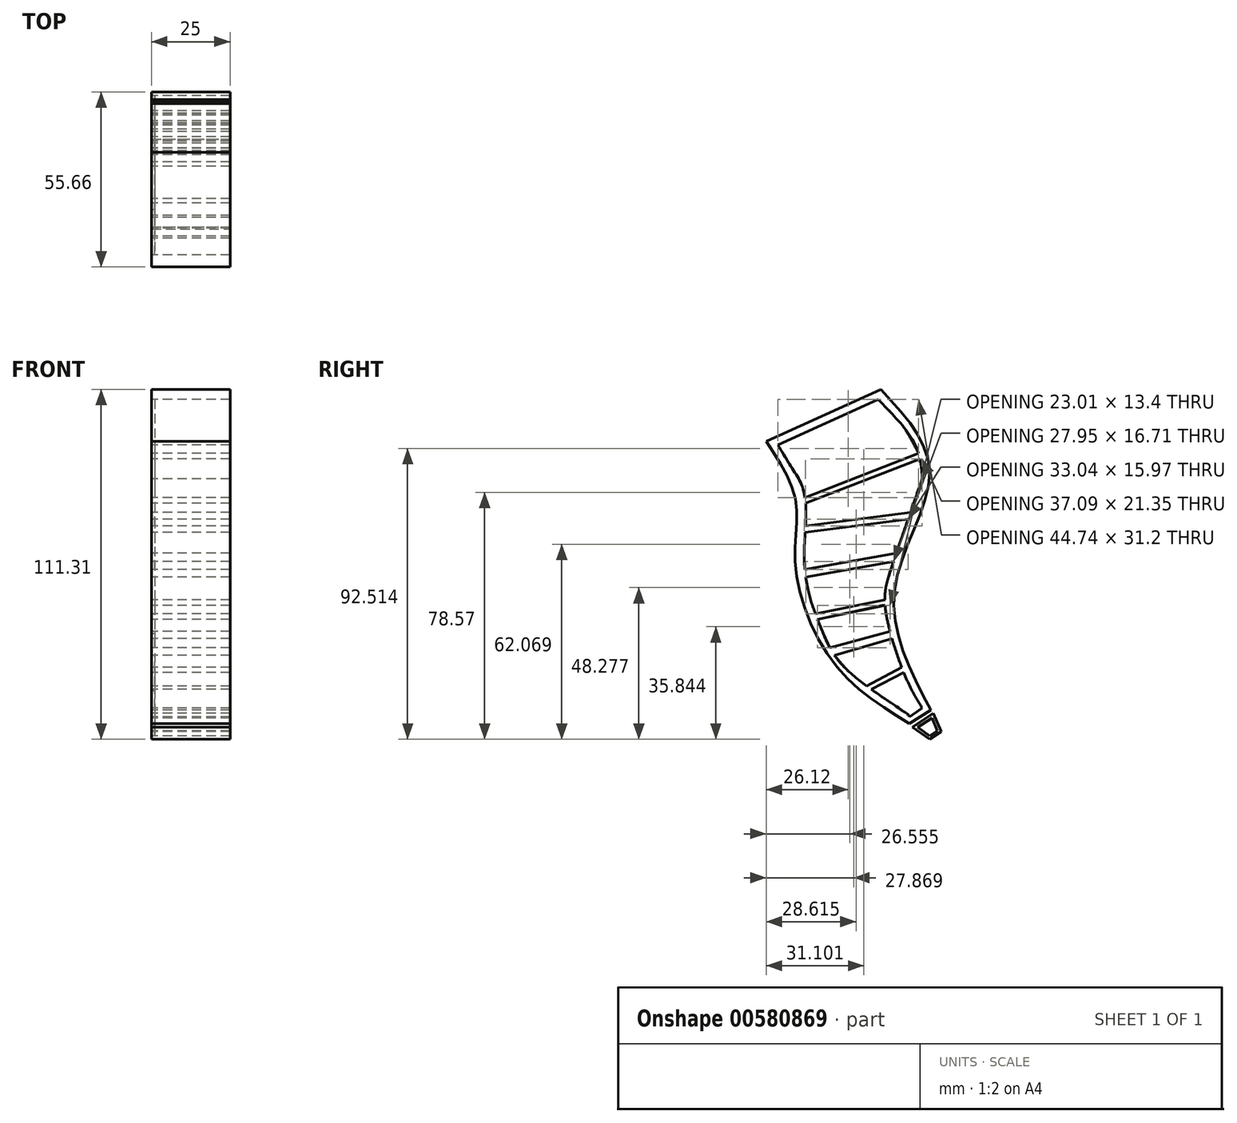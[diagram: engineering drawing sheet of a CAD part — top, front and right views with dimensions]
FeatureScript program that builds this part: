
annotation { "Feature Type Name" : "Feature", "Feature Type Description" : "" }
export const myFeature = defineFeature(function(context is Context, id is Id, definition is map)
    precondition{}
    {
        {
            var Q0;
            Q0=qCreatedBy(makeId("Right.planeOp"),FACE);
            var sketch = newSketch(context, id + "F0", { "sketchPlane" : qUnion([Q0])});
            skLineSegment(sketch, "E0", {"start": v(40.35, 35.98) * mm, "end": v(76.8, 52.44) * mm});
            skFitSpline(sketch, "E1", {"points": [v(40.35, 35.98) * mm, v(49.78, 17) * mm, v(49.59, -3.47) * mm, v(62.3, -35.09) * mm, v(85.9, -53.8) * mm], "startDerivative": vector(55.56, -83.92) * mm, "endDerivative": vector(95.14, -57.57) * mm});
            skFitSpline(sketch, "E2", {"points": [v(76.8, 52.44) * mm, v(92.3, 25.95) * mm, v(81.18, -11.43) * mm, v(92.7, -49.6) * mm], "startDerivative": vector(75.58, -81.14) * mm, "endDerivative": vector(56.5, -108.15) * mm});
            skLineSegment(sketch, "E3", {"start": v(85.9, -53.8) * mm, "end": v(92.7, -49.6) * mm});
            skLineSegment(sketch, "E4", {"start": v(44.1, 34.77) * mm, "end": v(75.97, 49.24) * mm});
            skFitSpline(sketch, "E5", {"points": [v(75.97, 49.24) * mm, v(87.81, 34.77) * mm, v(90, 24.03) * mm], "startDerivative": vector(25.4, -25.78) * mm, "endDerivative": vector(1.6, -24.6) * mm});
            skFitSpline(sketch, "E6", {"points": [v(90, 24.03) * mm, v(84.83, 9.32) * mm, v(79.67, -5.99) * mm, v(78.08, -14.54) * mm, v(80.86, -28.46) * mm, v(86.22, -42.37) * mm, v(90, -48.93) * mm], "startDerivative": vector(-27.15, -77) * mm, "endDerivative": vector(28.72, -45.43) * mm});
            skPoint(sketch, "E7.9.internal.snap0", {"position": v(89.3, -51.7) * mm});
            skFitSpline(sketch, "E7", {"points": [v(44.1, 34.77) * mm, v(48.47, 27.58) * mm, v(51.65, 22.04) * mm, v(53.04, 13.3) * mm, v(52.45, 0) * mm, v(54.04, -12.75) * mm, v(58.2, -24.48) * mm, v(66.75, -37.4) * mm, v(85.83, -51.32) * mm, v(86, -51.7) * mm], "startDerivative": vector(43.93, -74.3) * mm, "endDerivative": vector(0.94, -12.08) * mm});
            skFitSpline(sketch, "E8", {"points": [v(90, -48.93) * mm, v(86, -51.7) * mm], "startDerivative": vector(-3.97, -2.75) * mm, "endDerivative": vector(-3.97, -2.75) * mm});
            skLineSegment(sketch, "E9", {"start": v(73.75, -42.93) * mm, "end": v(84.1, -37.61) * mm});
            skLineSegment(sketch, "E10", {"start": v(72.29, -41.86) * mm, "end": v(83.45, -35.94) * mm});
            skLineSegment(sketch, "E11", {"start": v(52.9, 9.03) * mm, "end": v(86.22, 13.3) * mm});
            skLineSegment(sketch, "E12", {"start": v(52.78, 7) * mm, "end": v(85.48, 11.18) * mm});
            skLineSegment(sketch, "E13", {"start": v(60.61, -29.72) * mm, "end": v(79.72, -24.5) * mm});
            skLineSegment(sketch, "E14", {"start": v(62.1, -32.13) * mm, "end": v(80.38, -26.86) * mm});
            skLineSegment(sketch, "E15", {"start": v(52.9, 16.24) * mm, "end": v(89.27, 30.37) * mm});
            skLineSegment(sketch, "E16", {"start": v(52.69, 18.05) * mm, "end": v(88.84, 32.1) * mm});
            skLineSegment(sketch, "E17", {"start": v(86.87, -55) * mm, "end": v(93.55, -50.59) * mm});
            skLineSegment(sketch, "E18", {"start": v(86.87, -55) * mm, "end": v(92.3, -58.87) * mm});
            skLineSegment(sketch, "E19", {"start": v(92.3, -58.87) * mm, "end": v(96, -56.42) * mm});
            skLineSegment(sketch, "E20", {"start": v(96, -56.42) * mm, "end": v(93.55, -50.59) * mm});
            skLineSegment(sketch, "E21", {"start": v(88.55, -55) * mm, "end": v(93.06, -52.02) * mm});
            skLineSegment(sketch, "E22", {"start": v(93.06, -52.02) * mm, "end": v(94.8, -56.16) * mm});
            skLineSegment(sketch, "E23", {"start": v(94.8, -56.16) * mm, "end": v(92.3, -57.8) * mm});
            skLineSegment(sketch, "E24", {"start": v(92.3, -57.8) * mm, "end": v(88.55, -55) * mm});
            skLineSegment(sketch, "E25", {"start": v(52.93, -7.22) * mm, "end": v(80.88, -2.24) * mm});
            skLineSegment(sketch, "E26", {"start": v(52.65, -4.79) * mm, "end": v(81.76, 0.4) * mm});
            skLineSegment(sketch, "E27", {"start": v(56.71, -20.77) * mm, "end": v(77.27, -16.33) * mm});
            skLineSegment(sketch, "E28", {"start": v(56.02, -18.95) * mm, "end": v(78.08, -14.54) * mm});
            skLineSegment(sketch, "E29", {"start": v(77.27, -16.33) * mm, "end": v(78.17, -16.33) * mm});
            skSolve(sketch);
        }
        {
            var Q0;
            Q0 = qSketchRegion(id + "F0", true);
            extrude(context, id + "F1", {"entities" : qUnion([Q0]), "depth" : 25 * mm, "offsetDistance" : 25 * mm});
        }
        {
            var Q0;
            {var subQ0=sQuery(id+"F0.wireOp",EDGE,"E15");Q0=makeQuery(id+"F0.imprint","IMPRINT",FACE,{"disambiguationData":[TD([[makeQuery(id+"F0.imprint","IMPRINT",EDGE,{"derivedFrom":subQ0}),1.0]])]});}
            extrude(context, id + "F2", {"entities" : qUnion([Q0]), "operationType" : NewBodyOperationType.ADD, "depth" : 25 * mm, "offsetDistance" : 25 * mm});
        }
        {
            var Q0;
            {var subQ0=sQuery(id+"F0.wireOp",EDGE,"E11");Q0=makeQuery(id+"F0.imprint","IMPRINT",FACE,{"disambiguationData":[TD([[makeQuery(id+"F0.imprint","IMPRINT",EDGE,{"derivedFrom":subQ0}),-1.0]])]});}
            extrude(context, id + "F3", {"entities" : qUnion([Q0]), "operationType" : NewBodyOperationType.ADD, "depth" : 25 * mm, "offsetDistance" : 25 * mm});
        }
        {
            var Q0;
            {var subQ0=sQuery(id+"F0.wireOp",EDGE,"E25");Q0=makeQuery(id+"F0.imprint","IMPRINT",FACE,{"disambiguationData":[TD([[makeQuery(id+"F0.imprint","IMPRINT",EDGE,{"derivedFrom":subQ0}),1.0]])]});}
            extrude(context, id + "F4", {"entities" : qUnion([Q0]), "operationType" : NewBodyOperationType.ADD, "depth" : 25 * mm, "offsetDistance" : 25 * mm});
        }
        {
            var Q0;
            {var subQ1=sQuery(id+"F0.wireOp",EDGE,"E27");Q0=makeQuery(id+"F0.imprint","IMPRINT",FACE,{"disambiguationData":[TD([[makeQuery(id+"F0.imprint","IMPRINT",EDGE,{"derivedFrom":subQ1}),1.0]])]});}
            extrude(context, id + "F5", {"entities" : qUnion([Q0]), "operationType" : NewBodyOperationType.ADD, "depth" : 25 * mm, "offsetDistance" : 25 * mm});
        }
        {
            var Q0;
            {var subQ0=sQuery(id+"F0.wireOp",EDGE,"E13");Q0=makeQuery(id+"F0.imprint","IMPRINT",FACE,{"disambiguationData":[TD([[makeQuery(id+"F0.imprint","IMPRINT",EDGE,{"derivedFrom":subQ0}),-1.0]])]});}
            extrude(context, id + "F6", {"entities" : qUnion([Q0]), "operationType" : NewBodyOperationType.ADD, "depth" : 25 * mm, "offsetDistance" : 25 * mm});
        }
        {
            var Q0;
            {var subQ0=sQuery(id+"F0.wireOp",EDGE,"E9");Q0=makeQuery(id+"F0.imprint","IMPRINT",FACE,{"disambiguationData":[TD([[makeQuery(id+"F0.imprint","IMPRINT",EDGE,{"derivedFrom":subQ0}),1.0]])]});}
            extrude(context, id + "F7", {"entities" : qUnion([Q0]), "operationType" : NewBodyOperationType.ADD, "depth" : 25 * mm, "offsetDistance" : 25 * mm});
        }
        {
            var Q0;
            {var subQ0=sQuery(id+"F0.wireOp",EDGE,"E7");var subQ1=sQuery(id+"F0.wireOp",EDGE,"E6");var subQ2=sQuery(id+"F0.wireOp",EDGE,"E5");Q0=makeQuery(id+"F7.boolean.opBoolean","MERGE",FACE,{"derivedFrom":[makeQuery(id+"F6.boolean.opBoolean","MERGE",FACE,{"derivedFrom":[makeQuery(id+"F5.boolean.opBoolean","MERGE",FACE,{"derivedFrom":[makeQuery(id+"F4.boolean.opBoolean","MERGE",FACE,{"derivedFrom":[makeQuery(id+"F3.boolean.opBoolean","MERGE",FACE,{"derivedFrom":[makeQuery(id+"F2.boolean.opBoolean","MERGE",FACE,{"derivedFrom":[makeQuery(id+"F1.opExtrude","CAP_FACE",FACE,{"disambiguationData":[OSD([sQuery(id+"F0.wireOp",EDGE,"E0"),sQuery(id+"F0.wireOp",EDGE,"E1"),sQuery(id+"F0.wireOp",EDGE,"E2"),sQuery(id+"F0.wireOp",EDGE,"E3"),sQuery(id+"F0.wireOp",EDGE,"E4"),subQ2,subQ1,subQ0,sQuery(id+"F0.wireOp",EDGE,"E8")])],"isStart":true}),makeQuery(id+"F2.opExtrude","CAP_FACE",FACE,{"disambiguationData":[OSD([subQ2,subQ0,sQuery(id+"F0.wireOp",EDGE,"E15"),sQuery(id+"F0.wireOp",EDGE,"E16")])],"isStart":true})]}),makeQuery(id+"F3.opExtrude","CAP_FACE",FACE,{"disambiguationData":[OSD([subQ1,subQ0,sQuery(id+"F0.wireOp",EDGE,"E11"),sQuery(id+"F0.wireOp",EDGE,"E12")])],"isStart":true})]}),makeQuery(id+"F4.opExtrude","CAP_FACE",FACE,{"disambiguationData":[OSD([subQ1,subQ0,sQuery(id+"F0.wireOp",EDGE,"E25"),sQuery(id+"F0.wireOp",EDGE,"E26")])],"isStart":true})]}),makeQuery(id+"F5.opExtrude","CAP_FACE",FACE,{"disambiguationData":[OSD([subQ1,subQ0,sQuery(id+"F0.wireOp",EDGE,"E27"),sQuery(id+"F0.wireOp",EDGE,"E28"),sQuery(id+"F0.wireOp",EDGE,"E29")])],"isStart":true})]}),makeQuery(id+"F6.opExtrude","CAP_FACE",FACE,{"disambiguationData":[OSD([subQ1,subQ0,sQuery(id+"F0.wireOp",EDGE,"E13"),sQuery(id+"F0.wireOp",EDGE,"E14")])],"isStart":true})]}),makeQuery(id+"F7.opExtrude","CAP_FACE",FACE,{"disambiguationData":[OSD([subQ1,subQ0,sQuery(id+"F0.wireOp",EDGE,"E9"),sQuery(id+"F0.wireOp",EDGE,"E10")])],"isStart":true})]});}
            cPlane(context, id + "F8", {"entities" : qUnion([Q0]), "cplaneType" : CPlaneType.OFFSET, "offset" : 0 * mm, "width" : 150 * mm, "height" : 150 * mm});
        }
        {
            var Q0;
            Q0=qCreatedBy(id+"F8.planeOp",FACE);
            var sketch = newSketch(context, id + "F9", { "sketchPlane" : qUnion([Q0])});
            skPoint(sketch, "E30.0", {"position": v(-49.06, 26.7) * mm});
            skPoint(sketch, "E31.0", {"position": v(-75.97, 49.24) * mm});
            skPoint(sketch, "E32.0", {"position": v(-44.1, 34.77) * mm});
            skPoint(sketch, "E33.0", {"position": v(-52.69, 18.05) * mm});
            skPoint(sketch, "E34.0", {"position": v(-88.84, 32.1) * mm});
            skPoint(sketch, "E35.0", {"position": v(-89.27, 30.37) * mm});
            skPoint(sketch, "E36.0", {"position": v(-86.22, 13.3) * mm});
            skPoint(sketch, "E37.0", {"position": v(-52.9, 9.03) * mm});
            skPoint(sketch, "E38.0", {"position": v(-52.9, 16.24) * mm});
            skFitSpline(sketch, "E39", {"points": [v(-75.97, 49.24) * mm, v(-83.51, 41.21) * mm, v(-88.84, 32.1) * mm], "startDerivative": vector(-15.99, -15.24) * mm, "endDerivative": vector(-9.73, -19.07) * mm});
            skFitSpline(sketch, "E40", {"points": [v(-75.97, 49.24) * mm, v(-44.1, 34.77) * mm], "startDerivative": vector(31.87, -14.48) * mm, "endDerivative": vector(31.87, -14.48) * mm});
            skFitSpline(sketch, "E41", {"points": [v(-44.1, 34.77) * mm, v(-49.06, 26.7) * mm, v(-51.59, 22.32) * mm, v(-52.69, 18.05) * mm], "startDerivative": vector(-12.7, -21.07) * mm, "endDerivative": vector(-2.96, -15.55) * mm});
            skFitSpline(sketch, "E42", {"points": [v(-88.84, 32.1) * mm, v(-52.69, 18.05) * mm], "startDerivative": vector(36.15, -14.05) * mm, "endDerivative": vector(36.15, -14.05) * mm});
            skFitSpline(sketch, "E43", {"points": [v(-89.27, 30.37) * mm, v(-90.25, 24.39) * mm, v(-86.22, 13.3) * mm], "startDerivative": vector(-4.27, -13.36) * mm, "endDerivative": vector(9.61, -20.41) * mm});
            skFitSpline(sketch, "E44", {"points": [v(-89.27, 30.37) * mm, v(-52.9, 16.24) * mm], "startDerivative": vector(36.37, -14.13) * mm, "endDerivative": vector(36.37, -14.13) * mm});
            skFitSpline(sketch, "E45", {"points": [v(-52.9, 9.03) * mm, v(-86.22, 13.3) * mm], "startDerivative": vector(-33.32, 4.27) * mm, "endDerivative": vector(-33.32, 4.27) * mm});
            skFitSpline(sketch, "E46", {"points": [v(-52.9, 16.24) * mm, v(-52.9, 9.03) * mm], "startDerivative": vector(0, -7.22) * mm, "endDerivative": vector(0, -7.22) * mm});
            skPoint(sketch, "E47.0", {"position": v(-52.78, 7) * mm});
            skPoint(sketch, "E48.0", {"position": v(-52.46, 1.1) * mm});
            skPoint(sketch, "E49.0", {"position": v(-52.65, -4.79) * mm});
            skPoint(sketch, "E50.0", {"position": v(-81.76, 0.4) * mm});
            skPoint(sketch, "E51.0", {"position": v(-85.48, 11.18) * mm});
            skPoint(sketch, "E52.0", {"position": v(-69.13, 9.09) * mm});
            skPoint(sketch, "E53.0", {"position": v(-80.88, -2.24) * mm});
            skPoint(sketch, "E54.0", {"position": v(-78.98, -8.29) * mm});
            skPoint(sketch, "E55.0", {"position": v(-78.08, -14.54) * mm});
            skPoint(sketch, "E56.0", {"position": v(-56.02, -18.95) * mm});
            skPoint(sketch, "E57.0", {"position": v(-54.15, -13.17) * mm});
            skPoint(sketch, "E58.0", {"position": v(-52.93, -7.22) * mm});
            skPoint(sketch, "E59.0", {"position": v(-78.17, -16.33) * mm});
            skPoint(sketch, "E60.0", {"position": v(-56.71, -20.77) * mm});
            skPoint(sketch, "E61.0", {"position": v(-60.61, -29.72) * mm});
            skPoint(sketch, "E62.0", {"position": v(-58.55, -25.3) * mm});
            skPoint(sketch, "E63.0", {"position": v(-78.78, -20.44) * mm});
            skPoint(sketch, "E64.0", {"position": v(-79.72, -24.5) * mm});
            skPoint(sketch, "E65.0", {"position": v(-80.38, -26.86) * mm});
            skPoint(sketch, "E66.0", {"position": v(-62.1, -32.13) * mm});
            skPoint(sketch, "E67.0", {"position": v(-66.78, -37.42) * mm});
            skPoint(sketch, "E68.0", {"position": v(-72.29, -41.86) * mm});
            skPoint(sketch, "E69.0", {"position": v(-83.45, -35.94) * mm});
            skPoint(sketch, "E70.0", {"position": v(-84.1, -37.61) * mm});
            skPoint(sketch, "E71.0", {"position": v(-73.75, -42.93) * mm});
            skPoint(sketch, "E72.0", {"position": v(-90, -48.93) * mm});
            skPoint(sketch, "E73.0", {"position": v(-86, -51.7) * mm});
            skPoint(sketch, "E74.0", {"position": v(-80, -47.2) * mm});
            skPoint(sketch, "E75.0", {"position": v(-86.76, -43.43) * mm});
            skPoint(sketch, "E76.0", {"position": v(-93.06, -52.02) * mm});
            skPoint(sketch, "E77.0", {"position": v(-88.55, -55) * mm});
            skPoint(sketch, "E78.0", {"position": v(-92.3, -57.8) * mm});
            skPoint(sketch, "E79.0", {"position": v(-94.8, -56.16) * mm});
            skFitSpline(sketch, "E80", {"points": [v(-85.48, 11.18) * mm, v(-81.76, 0.4) * mm], "startDerivative": vector(3.72, -10.78) * mm, "endDerivative": vector(3.72, -10.78) * mm});
            skFitSpline(sketch, "E81", {"points": [v(-52.65, -4.79) * mm, v(-81.76, 0.4) * mm], "startDerivative": vector(-29.11, 5.19) * mm, "endDerivative": vector(-29.11, 5.19) * mm});
            skFitSpline(sketch, "E82", {"points": [v(-85.48, 11.18) * mm, v(-52.78, 7) * mm], "startDerivative": vector(32.7, -4.2) * mm, "endDerivative": vector(32.7, -4.2) * mm});
            skFitSpline(sketch, "E83", {"points": [v(-52.78, 7) * mm, v(-52.46, 1.1) * mm, v(-52.65, -4.79) * mm], "startDerivative": vector(0.87, -11.77) * mm, "endDerivative": vector(-0.62, -11.78) * mm});
            skFitSpline(sketch, "E84", {"points": [v(-80.88, -2.24) * mm, v(-52.93, -7.22) * mm], "startDerivative": vector(27.95, -4.98) * mm, "endDerivative": vector(27.95, -4.98) * mm});
            skFitSpline(sketch, "E85", {"points": [v(-52.93, -7.22) * mm, v(-54.15, -13.17) * mm, v(-56.02, -19.11) * mm], "startDerivative": vector(-2.14, -12.02) * mm, "endDerivative": vector(-4.05, -11.77) * mm});
            skFitSpline(sketch, "E86", {"points": [v(-80.88, -2.24) * mm, v(-78.98, -8.29) * mm, v(-78.08, -14.54) * mm], "startDerivative": vector(4.3, -11.98) * mm, "endDerivative": vector(1.3, -12.63) * mm});
            skFitSpline(sketch, "E87", {"points": [v(-78.08, -14.54) * mm, v(-56.02, -18.95) * mm], "startDerivative": vector(22.05, -4.41) * mm, "endDerivative": vector(22.05, -4.41) * mm});
            skFitSpline(sketch, "E88", {"points": [v(-78.17, -16.33) * mm, v(-56.71, -20.77) * mm], "startDerivative": vector(21.46, -4.44) * mm, "endDerivative": vector(21.46, -4.44) * mm});
            skFitSpline(sketch, "E89", {"points": [v(-78.17, -16.33) * mm, v(-79.72, -24.5) * mm], "startDerivative": vector(-1.55, -8.17) * mm, "endDerivative": vector(-1.55, -8.17) * mm});
            skFitSpline(sketch, "E90", {"points": [v(-79.72, -24.5) * mm, v(-60.61, -29.72) * mm], "startDerivative": vector(19.1, -5.22) * mm, "endDerivative": vector(19.1, -5.22) * mm});
            skFitSpline(sketch, "E91", {"points": [v(-56.71, -20.77) * mm, v(-58.55, -25.3) * mm], "startDerivative": vector(-1.83, -4.53) * mm, "endDerivative": vector(-1.83, -4.53) * mm});
            skFitSpline(sketch, "E92", {"points": [v(-60.61, -29.72) * mm, v(-58.55, -25.3) * mm], "startDerivative": vector(2.07, 4.43) * mm, "endDerivative": vector(2.07, 4.43) * mm});
            skFitSpline(sketch, "E93", {"points": [v(-80.38, -26.86) * mm, v(-83.45, -35.94) * mm], "startDerivative": vector(-3.07, -9.08) * mm, "endDerivative": vector(-3.07, -9.08) * mm});
            skFitSpline(sketch, "E94", {"points": [v(-83.45, -35.94) * mm, v(-72.29, -41.86) * mm], "startDerivative": vector(11.16, -5.92) * mm, "endDerivative": vector(11.16, -5.92) * mm});
            skFitSpline(sketch, "E95", {"points": [v(-72.29, -41.86) * mm, v(-66.78, -37.42) * mm, v(-62.1, -32.13) * mm], "startDerivative": vector(11.42, 8.46) * mm, "endDerivative": vector(8.96, 11) * mm});
            skFitSpline(sketch, "E96", {"points": [v(-80.38, -26.86) * mm, v(-62.1, -32.13) * mm], "startDerivative": vector(18.28, -5.27) * mm, "endDerivative": vector(18.28, -5.27) * mm});
            skFitSpline(sketch, "E97", {"points": [v(-84.1, -37.61) * mm, v(-73.75, -42.93) * mm], "startDerivative": vector(10.36, -5.32) * mm, "endDerivative": vector(10.36, -5.32) * mm});
            skFitSpline(sketch, "E98", {"points": [v(-73.75, -42.93) * mm, v(-86, -51.7) * mm], "startDerivative": vector(-12.25, -8.78) * mm, "endDerivative": vector(-12.25, -8.78) * mm});
            skFitSpline(sketch, "E99", {"points": [v(-90, -48.93) * mm, v(-86, -51.7) * mm], "startDerivative": vector(4, -2.77) * mm, "endDerivative": vector(4, -2.77) * mm});
            skFitSpline(sketch, "E100", {"points": [v(-90, -48.93) * mm, v(-86.76, -43.43) * mm], "startDerivative": vector(3.24, 5.5) * mm, "endDerivative": vector(3.24, 5.5) * mm});
            skFitSpline(sketch, "E101", {"points": [v(-84.1, -37.61) * mm, v(-86.76, -43.43) * mm], "startDerivative": vector(-2.65, -5.82) * mm, "endDerivative": vector(-2.65, -5.82) * mm});
            skFitSpline(sketch, "E102", {"points": [v(-93.06, -52.02) * mm, v(-88.55, -55) * mm], "startDerivative": vector(4.5, -2.97) * mm, "endDerivative": vector(4.5, -2.97) * mm});
            skFitSpline(sketch, "E103", {"points": [v(-88.55, -55) * mm, v(-92.3, -57.8) * mm], "startDerivative": vector(-3.75, -2.8) * mm, "endDerivative": vector(-3.75, -2.8) * mm});
            skFitSpline(sketch, "E104", {"points": [v(-92.3, -57.8) * mm, v(-94.8, -56.16) * mm], "startDerivative": vector(-2.5, 1.64) * mm, "endDerivative": vector(-2.5, 1.64) * mm});
            skFitSpline(sketch, "E105", {"points": [v(-94.8, -56.16) * mm, v(-93.06, -52.02) * mm], "startDerivative": vector(1.74, 4.14) * mm, "endDerivative": vector(1.74, 4.14) * mm});
            skLineSegment(sketch, "E106", {"start": v(-78.08, -14.54) * mm, "end": v(-56.02, -19.11) * mm});
            skSolve(sketch);
        }
        {
            var Q0;
            Q0 = qSketchRegion(id + "F9", true);
            extrude(context, id + "F10", {"entities" : qUnion([Q0]), "oppositeDirection" : true, "depth" : 1 * mm, "offsetDistance" : 25 * mm});
        }
        {
            var Q0;
            Q0 = qSketchRegion(id + "F9", true);
            extrude(context, id + "F11", {"entities" : qUnion([Q0]), "oppositeDirection" : true, "depth" : 1 * mm, "offsetDistance" : 25 * mm});
        }
    });
